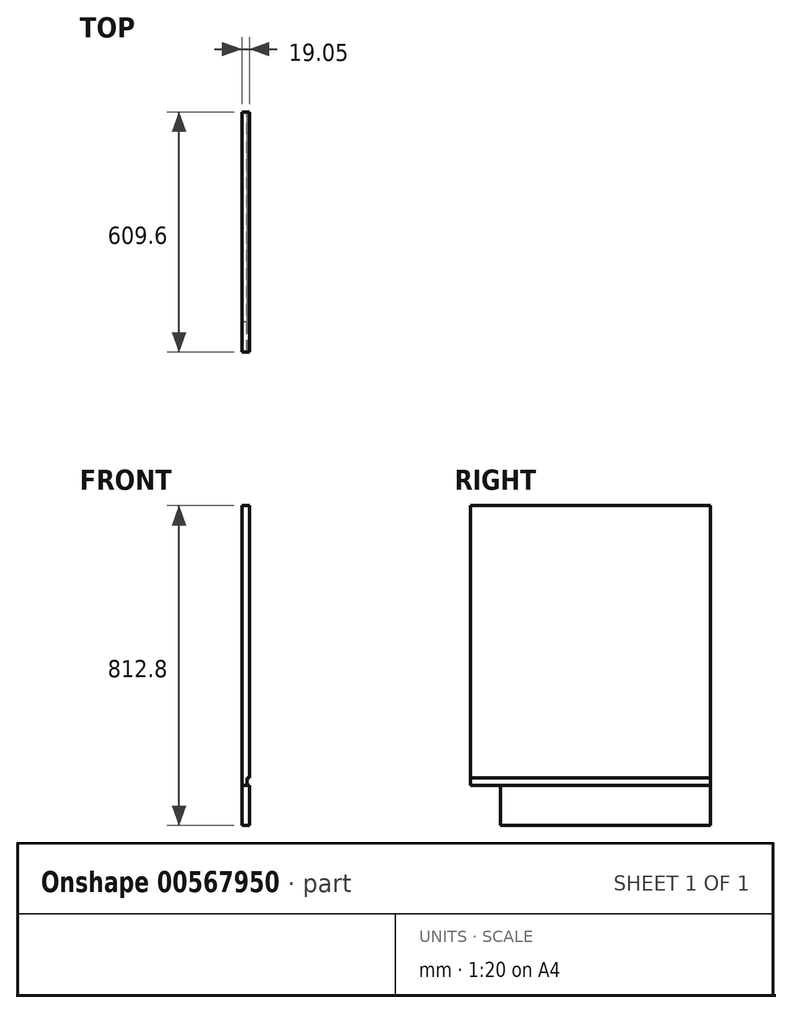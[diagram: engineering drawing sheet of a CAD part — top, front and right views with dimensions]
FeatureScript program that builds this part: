
annotation { "Feature Type Name" : "Feature", "Feature Type Description" : "" }
export const myFeature = defineFeature(function(context is Context, id is Id, definition is map)
    precondition{}
    {
        {
            var Q0;
            Q0=qCreatedBy(makeId("Right.planeOp"),FACE);
            var sketch = newSketch(context, id + "F0", { "sketchPlane" : qUnion([Q0])});
            skLineSegment(sketch, "E0", {"start": v(0, 0) * mm, "end": v(0, 101.6) * mm});
            skLineSegment(sketch, "E1", {"start": v(0, 101.6) * mm, "end": v(-76.2, 101.6) * mm});
            skLineSegment(sketch, "E2", {"start": v(-76.2, 101.6) * mm, "end": v(-76.2, 812.8) * mm});
            skLineSegment(sketch, "E3", {"start": v(-76.2, 812.8) * mm, "end": v(533.4, 812.8) * mm});
            skLineSegment(sketch, "E4", {"start": v(533.4, 812.8) * mm, "end": v(533.4, 0) * mm});
            skLineSegment(sketch, "E5", {"start": v(533.4, 0) * mm, "end": v(0, 0) * mm});
            skSolve(sketch);
        }
        {
            var Q0;
            Q0=qSketchRegion(id+"F0",true);
            extrude(context, id + "F1", {"entities" : qUnion([Q0]), "depth" : 19.05 * mm, "offsetDistance" : 25.4 * mm});
        }
        {
            var Q0;
            Q0=makeQuery(id+"F1.opExtrude","CAP_FACE",FACE,{"disambiguationData":[OSD([sQuery(id+"F0.wireOp",EDGE,"E0"),sQuery(id+"F0.wireOp",EDGE,"E1"),sQuery(id+"F0.wireOp",EDGE,"E2"),sQuery(id+"F0.wireOp",EDGE,"E3"),sQuery(id+"F0.wireOp",EDGE,"E4"),sQuery(id+"F0.wireOp",EDGE,"E5")])],"isStart":false});
            var sketch = newSketch(context, id + "F2", { "sketchPlane" : qUnion([Q0])});
            skLineSegment(sketch, "E6.bottom", {"start": v(-76.2, 101.6) * mm, "end": v(533.4, 101.6) * mm});
            skLineSegment(sketch, "E6.top", {"start": v(-76.2, 120.65) * mm, "end": v(533.4, 120.65) * mm});
            skLineSegment(sketch, "E6.left", {"start": v(-76.2, 101.6) * mm, "end": v(-76.2, 120.65) * mm});
            skLineSegment(sketch, "E6.right", {"start": v(533.4, 101.6) * mm, "end": v(533.4, 120.65) * mm});
            skSolve(sketch);
        }
        {
            var Q0;
            Q0=makeQuery(id+"F2.imprint","IMPRINT",FACE,{"disambiguationData":[TD([[makeQuery(id+"F2.imprint","IMPRINT",EDGE,{"derivedFrom":sQuery(id+"F2.wireOp",EDGE,"E6.top")}),-1.0]])]});
            extrude(context, id + "F3", {"entities" : qUnion([Q0]), "operationType" : NewBodyOperationType.REMOVE, "oppositeDirection" : true, "depth" : 6.35 * mm, "offsetDistance" : 25.4 * mm});
        }
    });
